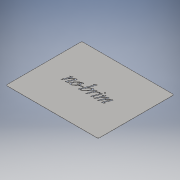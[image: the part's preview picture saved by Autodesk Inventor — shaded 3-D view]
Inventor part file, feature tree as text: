
AUTODESK INVENTOR PART (.ipt)
format: ipt  version: 2018 (Build 220112000, 112)  size: 443,904 bytes
history: native  units: mm
features: other x3, sketch x2, extrude x1
ambient origin geometry x8: Origin, YZ Plane, XZ Plane, XY Plane, X Axis, Y Axis, Z Axis, Center Point
bodies: Solido1 (feature_tree)
feature tree (6):
  other  "Faccia1"
  other  "Arrotondamento angolo1"
  extrude  "Estrusione1"  Depth=670.0mm
  sketch  "Schizzo1"
  other  "Piano1"
  sketch  "Schizzo2"
